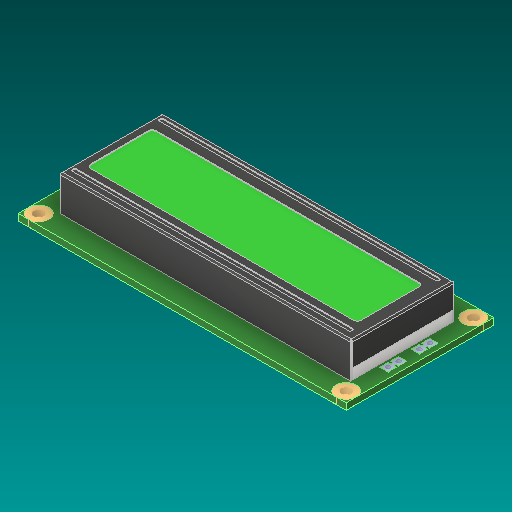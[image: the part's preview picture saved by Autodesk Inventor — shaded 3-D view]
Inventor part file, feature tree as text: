
AUTODESK INVENTOR PART (.ipt)
format: ipt  version: 2019 (Build 230136000, 136)  size: 566,784 bytes
history: native  units: mm
features: other x31, fillet x3
ambient origin geometry x8: Origin, YZ Plane, XZ Plane, XY Plane, X Axis, Y Axis, Z Axis, Center Point
bodies: Solid1 (feature_tree), Solid2 (feature_tree), Solid3 (feature_tree), Solid4 (feature_tree), Solid5 (feature_tree), Solid6 (feature_tree), Solid7 (feature_tree), Solid8 (feature_tree), Solid9 (feature_tree), Solid10 (feature_tree), Solid11 (feature_tree), Solid12 (feature_tree), Solid13 (feature_tree), Solid14 (feature_tree), Solid15 (feature_tree), Solid16 (feature_tree), Solid17 (feature_tree), Solid18 (feature_tree), Solid19 (feature_tree), Solid20 (feature_tree), Solid21 (feature_tree), Solid22 (feature_tree), Solid23 (feature_tree), Solid24 (feature_tree), Solid25 (feature_tree), Solid26 (feature_tree), Solid27 (feature_tree), Solid28 (feature_tree), Solid29 (feature_tree), Solid30 (feature_tree), Solid31 (feature_tree), Solid32 (feature_tree), Solid33 (feature_tree), Solid34 (feature_tree)
feature tree (34):
  other  "Cut-Extrude2"
  other  "Boss-Extrude3"
  other  "Boss-Extrude7[1]"
  other  "Boss-Extrude7[2]"
  other  "Boss-Extrude7[3]"
  other  "Boss-Extrude7[4]"
  other  "Boss-Extrude7[5]"
  other  "LPattern3[1]"
  other  "LPattern3[2]"
  other  "LPattern3[3]"
  other  "LPattern3[4]"
  other  "LPattern3[5]"
  other  "LPattern3[6]"
  other  "LPattern3[7]"
  other  "LPattern3[8]"
  other  "LPattern3[9]"
  other  "LPattern3[10]"
  other  "LPattern3[11]"
  other  "LPattern3[12]"
  other  "LPattern3[13]"
  other  "LPattern3[14]"
  other  "LPattern3[15]"
  fillet  "Fillet5"  [1 undecoded]
  fillet  "Fillet7"  [1 undecoded]
  fillet  "Fillet9"  [1 undecoded]
  other  "Boss-Extrude9[1]"
  other  "Boss-Extrude9[2]"
  other  "Boss-Extrude9[3]"
  other  "Boss-Extrude9[4]"
  other  "Boss-Extrude9[5]"
  other  "Boss-Extrude9[6]"
  other  "Cut-Extrude6"
  other  "Boss-Extrude12[1]"
  other  "Boss-Extrude12[2]"
note: 3 required parameter values undecoded (feature->parameter linkage not recoverable at this tier; creation-order binding heuristic only, values carry confidence <= 0.55)
